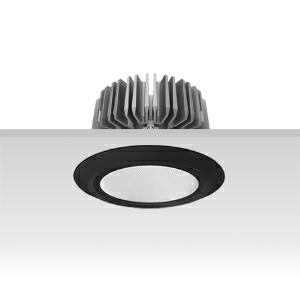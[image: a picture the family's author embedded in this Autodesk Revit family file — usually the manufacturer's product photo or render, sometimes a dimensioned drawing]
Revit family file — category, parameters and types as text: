
# Revit family: 3f_filippi_-_3f_reno_bianco_ampio_3f_filippi_-_30383_a01047_-_3f_reno_150_wh_3000-840_dali_wide___smp_bk_8a26
name_source: partatom
category: Lighting Fixtures
units: mm (PartAtom-declared; Revit-internal decimal feet)

## family parameters
Cut with Voids When Loaded = No
Host = Face
Light Source = No
Part Type = Normal
Room Calculation Point = No
Round Connector Dimension = Use Diameter
Shared = No

## types (1)
- 3F Filippi - 3F Reno Bianco Ampio (1 x LED, 2316 lm, 28 W, 4000 K)
    Apparent Load = 28 VA
    Approval mark = CE
    CIE Flux Codes = 73 92 98 100 100
    Color Rendering = 80
    Color Temperature = 4000 K
    Control Gear = Electronic transformer
    Default Elevation = 1800 mm
    Description = ILLUMINOTECHNICAL
Luminous efficiency 100% (DLOR 100%, ULOR 0%).
Initial luminous flux of the luminaire 2316 lm.
Direct symmetric wide distribution.
Installation Interdistance Transv.D = 1.01 x hu - Long.D = 1.00 x hu.
Tabular UGR (CIE 117 - 4H-8H; S=0.25H; 70/50/20): RUG 24.4 - 24.5.
Beam angle: 70° - 70°.
Luminous efficacy 83 lm/W.
Lifetime (L90/B10): 30000 h. (tq+25°C)
Lifetime (L85/B10): 50000 h. (tq+25°C)
Lifetime (L70/B10): 80000 h. (tq+25°C)
Sudden decreased luminous flux after 50000 hours: 0% (C0).
Photobiological safety in compliance with IEC/TR 62778: RG0 risk exempt, (IEC 62471).
In compliance with IEC/EN 62722-2-1 - IEC/EN 62717 standards.

SOURCE
Compact LED module 3000/840.
Energy efficiency class (UE 2019/2020 - UE 2019/2015): E.
CIE 13.3 Colour rendering index: CRI >80 (R9 <50%).
IES TM-30 Fidelity Index: Rf = 84 Rg = 95.
CCT nominal colour temperature 4000 K.
Colour initial tolerance (MacAdam): SDCM 3.
Zhaga Book 3 compliant.

MECHANICAL
Passive heat dissipator in die-casting aluminium, oversized, for optimum thermal management of the LED module.
Parabolic element with graduated/concentric rings in white polycarbonate.
Transparent external lens with glossy and satin differentiated surfaces, with a cooling and anti-insect system in methacrylate (PMMA).
Fastening spring clips in stainless steel.
Dimensions: diameter 176 mm, height 111 mm. Weight 1.34 kg.
IP44 protection degree for exposed part, IP20 for recessed part.
Mechanical strength to impacts IK05 (0.7 joule).
Glow-wire test resistance 650°C.

ELECTRICAL
Wiring on a separate unit.
Halogen Free DALI-2 DATI (Parts 251, 252, 253), PUSH-DIM, electronic wiring 230V-50/60Hz, power factor 0.97 at full load, THD <25%, constant output current, SELV, class II, 1 driver, 1 DALI addresse.
Power of the luminaire 28 W.
ENEC - CE.
SAFE FLICKER: PstLM=<1 and SVM=<0.4 (IEC TR 61547-1 and IEC TR 63158), to ensure a more comfortable and safe light.
Luminaire compliant with EN 60598-2-22 for power supply from a centralised emergency system CPSS (Central Power Supply System), not incorporated in the luminaire - high risk areas excluded. The default power and flux are 100% in AC and 100% in DC.
Ambient temperature from 0°C to +25°C.
Temperature class T6 max 85°C.
Relative humidity UR: <85%.

INSTALLATION
Pull-up recessed fitting.
False ceiling carving: 150 mm.
All accessories dedicated to this product are available on the Catalog and on our website www.3F-Filippi.com.

ACCESSORIES
A01047 - Anti-glare microprismatic SMP diffuser in methacrylate (PMMA), locked and in line with the trim, in black polycarbonate.

APPLICATIONS
Suitable product for food production plants (HACCP), IFS (Food Version 6), BRC (GSFS Food Version 7).
Environments: architectural, commercial, exhibition areas, transit areas, corridors, shops, display windows, service areas.
In false ceilings with narrow voids.

LIGHT MANAGEMENT
Recommended minimum setting: 10%.
The luminaire, equipped with (DALI-2 DATI) driver, can be controlled manually with 3F Easy Dim technology or automatically/manually with wired or wireless DALI/D2D control systems.
The D2D driver guarantees interoperability with other devices with the same certification by making the following information available:
Device Data (Part 251), Energy Report (Part 252), Diagnosis & Maintenance (Part 253).
In electrical systems without a regulation system (manual or automatic) and DALI bus, a suitable jumper must be made on the DA-DA terminals of the appliance.

WARNING
Luminaire designed for disposal/recycling at end-of-life.
Replaceable (LED only) light source by a professional. Replaceable control gear by a professional.
    Height = 0 mm  [stored 0 ft]
    Lamp = 1 x LED
    Lamp Light Flux = 2316 lm
    Lamp Power = 28 W
    Lamp count = 1
    Length = 176 mm
    Lifetime = 50000 h
    Luminous efficacy = 83 lm/W
    Manufacturer = 3F Filippi
    ModVariant = No
    Model = 3F Filippi - 30383+A01047 - 3F Reno 150 WH 3000-840 DALI WIDE + SMP BK
    Mounting Place = Ceiling
    Mounting Type = Recessed
    Number of Poles = 1
    OnlyDefault = Yes
    Power Factor = 1
    Product Name = 3F Filippi - 3F Reno Bianco Ampio
    Product group = recessed luminaire
    ProductGroupID = 4
    Protection Class = Protection class II
    Protection Degree = IP 20
    RLX_Detail_Level = 1
    RLX_Emergency_Light_Flux = 0 lm
    RLX_Emergency_Type = 0
    RLX_Emergency_Type_DB = No
    RlxData = <blob elided: 89433 chars, md5=19dff42e>
    Socket = socket
    Standby Power = 0 W
    System Light Flux = 2316 lm
    System Power = 28 W
    Type Comments = Product without accessories
    Type Image = 3ffilippi_3f_reno_150_bk_vs_smp.jpg
    URL = http://relux.com
    VarID = ---
    Voltage = 0 V
    Weight = 0.00 kg
    Width = 0 mm  [stored 0 ft]

note: [stored X ft] marks values corroborated as IEEE doubles in the binary element streams (Revit-internal decimal feet)

## geometry (parser evidence)
native form markers: Blend x4, Sweep x11
no freeform markers — native parametric forms only
